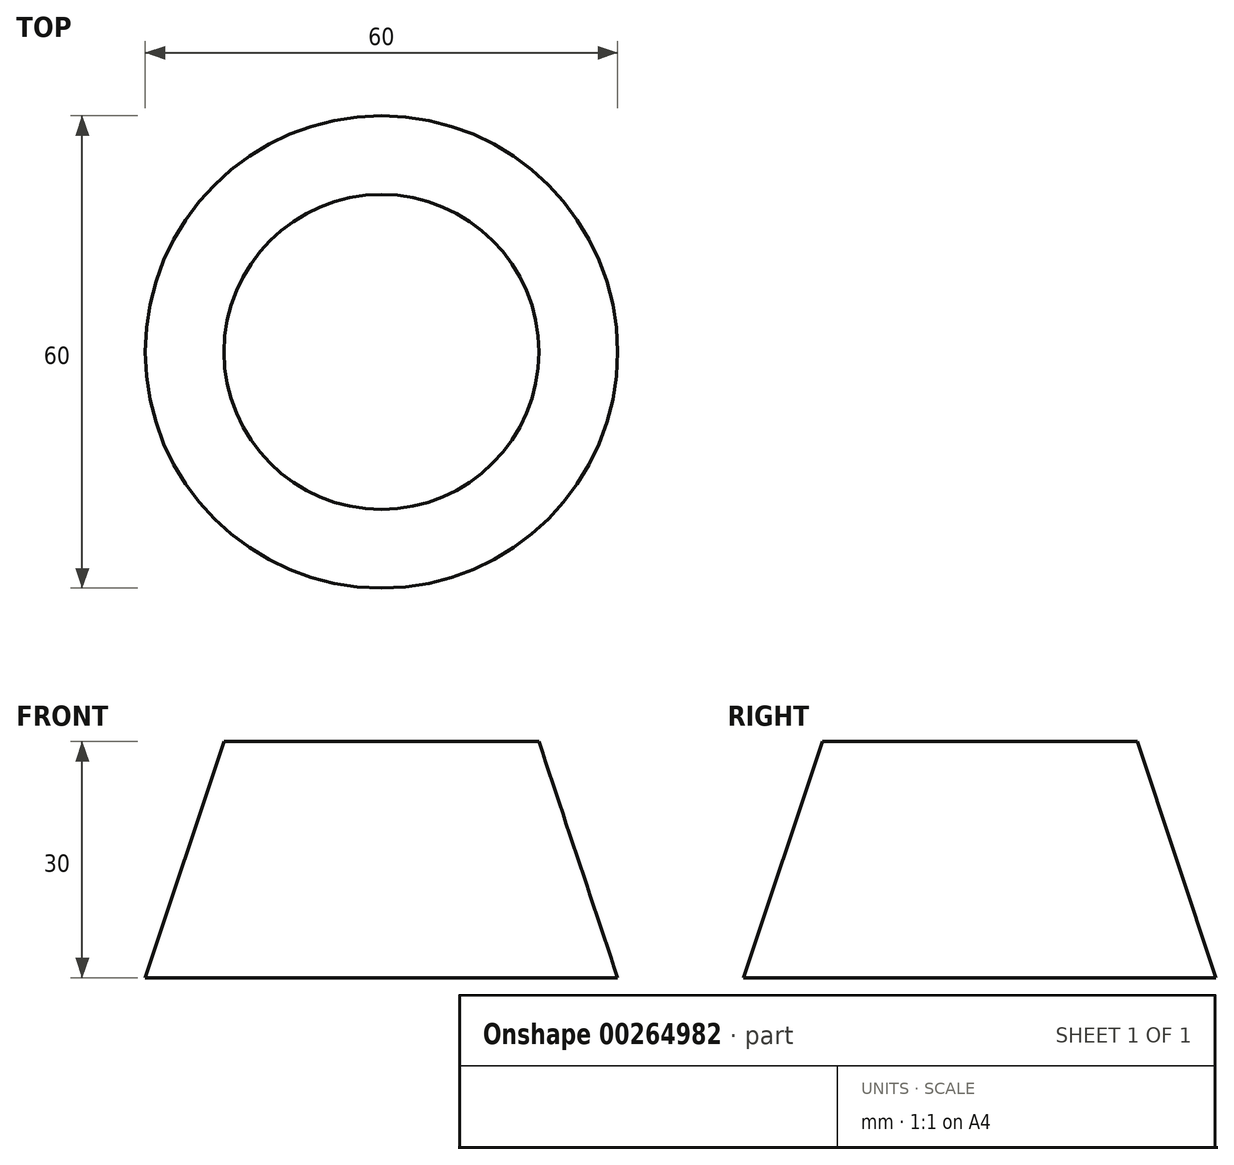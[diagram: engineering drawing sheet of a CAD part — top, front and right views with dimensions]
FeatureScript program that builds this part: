
annotation { "Feature Type Name" : "Feature", "Feature Type Description" : "" }
export const myFeature = defineFeature(function(context is Context, id is Id, definition is map)
    precondition{}
    {
        {
            var Q0;
            Q0=qCreatedBy(makeId("Front.planeOp"),FACE);
            var sketch = newSketch(context, id + "F0", { "sketchPlane" : qUnion([Q0])});
            skLineSegment(sketch, "E0", {"start": v(0, 0) * mm, "end": v(0, 30) * mm});
            skLineSegment(sketch, "E1", {"start": v(0, 30) * mm, "end": v(20, 30) * mm});
            skLineSegment(sketch, "E2", {"start": v(20, 30) * mm, "end": v(30, 0) * mm});
            skLineSegment(sketch, "E3", {"start": v(30, 0) * mm, "end": v(0, 0) * mm});
            skLineSegment(sketch, "E4", {"start": v(0, 45.9) * mm, "end": v(0, -29.46) * mm, "construction": true});
            skSolve(sketch);
        }
        {
            var Q0;
            Q0=makeQuery(id+"F0.imprint","IMPRINT",FACE,{"disambiguationData":[TD([[makeQuery(id+"F0.imprint","IMPRINT",EDGE,{"derivedFrom":sQuery(id+"F0.wireOp",EDGE,"E0")}),-1.0]])]});
            var Q1;
            Q1=sQuery(id+"F0.wireOp",EDGE,"E4");
            var Q2;
            Q2=sQuery(id+"F0.wireOp",EDGE,"E4");
            revolve(context, id + "F1", {"entities" : qUnion([Q0]), "surfaceEntities" : qUnion([Q1]), "axis" : qUnion([Q2]), "revolveType" : RevolveType.FULL});
        }
    });
